# Revit family: FU_Chair_Sandler_Light 1-3
name_source: partatom
category: Furniture
units: mm (PartAtom-declared; Revit-internal decimal feet)

## family parameters
Always vertical = Yes
Cut with Voids When Loaded = No
OmniClass Number = 23.40.20.00
OmniClass Title = General Furniture and Specialties
Room Calculation Point = No
Shared = No
Work Plane-Based = No

## types (1)
- Light 1.3
    Default Elevation = 0 mm  [stored 0 ft]
    Depth = 620 mm  [stored 2.03412 ft]
    Description = Upholstered side chair with a pleated upholstered shell on a solid beech frame.
    Frame = Wood - Beech - Light Walnut
    Height = 805 mm  [stored 2.64108 ft]
    Manufacturer = Sandler
    Model = Light 1.3
    Seat = Fabric - Manhattan - Bronx YI364
    URL = https://www.sandlerseating.com
    Width = 460 mm  [stored 1.50919 ft]

note: [stored X ft] marks values corroborated as IEEE doubles in the binary element streams (Revit-internal decimal feet)

## geometry (parser evidence)
native form markers: Sweep x4
no freeform markers — native parametric forms only
